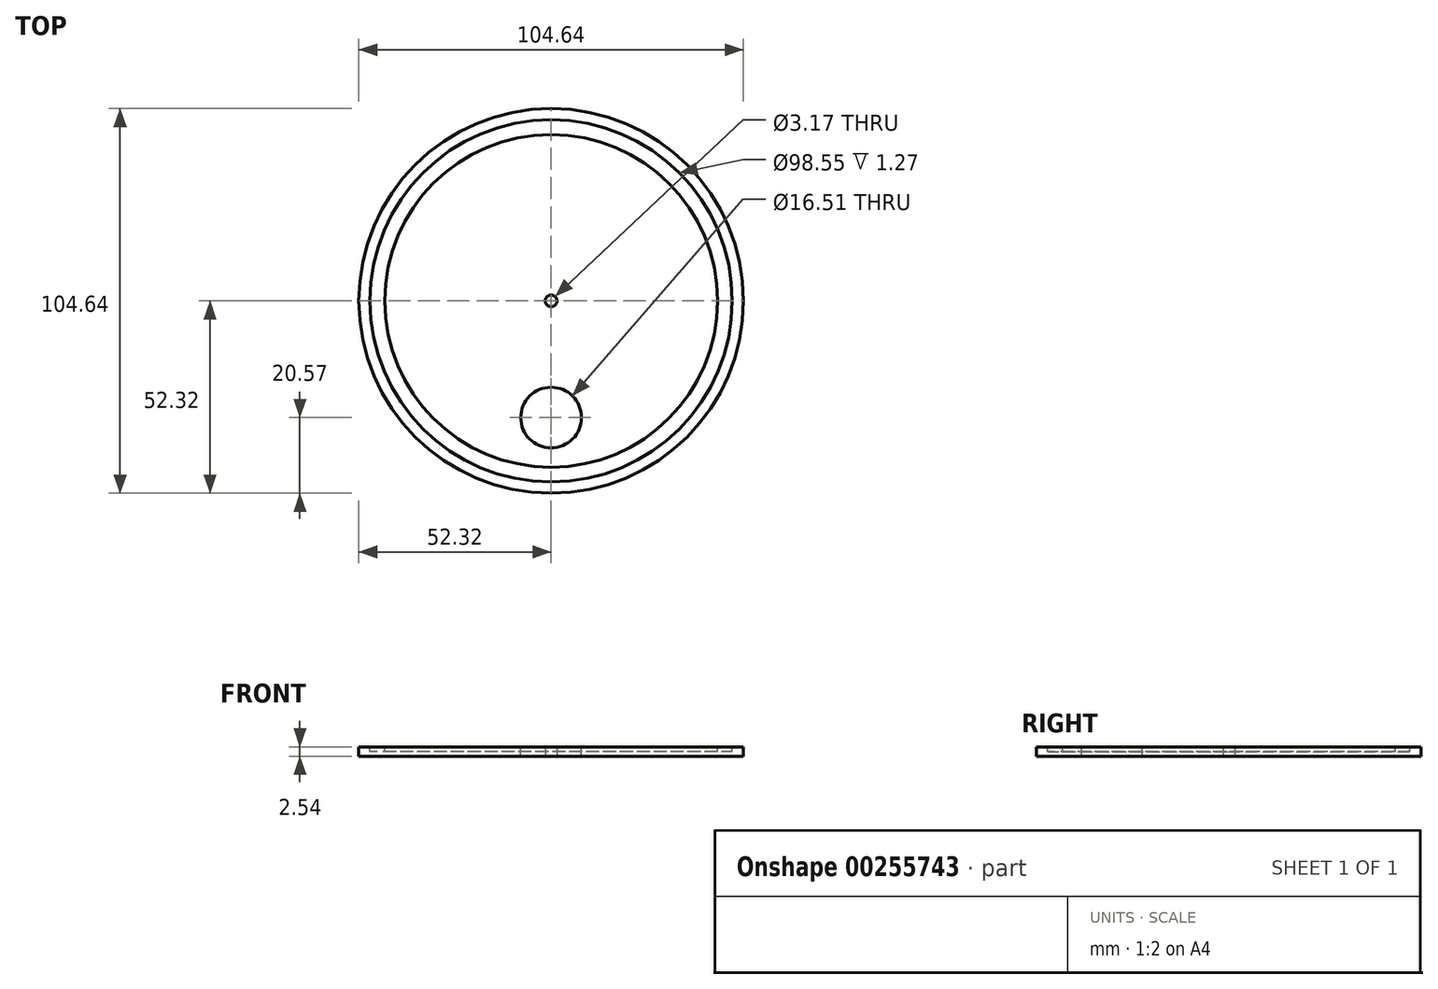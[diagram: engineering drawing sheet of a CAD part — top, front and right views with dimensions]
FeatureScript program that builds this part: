
annotation { "Feature Type Name" : "Feature", "Feature Type Description" : "" }
export const myFeature = defineFeature(function(context is Context, id is Id, definition is map)
    precondition{}
    {
        {
            var Q0;
            Q0=qCreatedBy(makeId("Top.planeOp"),FACE);
            var sketch = newSketch(context, id + "F0", { "sketchPlane" : qUnion([Q0])});
            skCircle(sketch, "E0", {"center": v(0, 0) * mm, "radius": 52.32 * mm});
            skCircle(sketch, "E1", {"center": v(0, 0) * mm, "radius": 1.59 * mm});
            skSolve(sketch);
        }
        {
            var Q0;
            Q0=makeQuery(id+"F0.imprint","IMPRINT",FACE,{"disambiguationData":[TD([[makeQuery(id+"F0.imprint","IMPRINT",EDGE,{"derivedFrom":sQuery(id+"F0.wireOp",EDGE,"E0")}),1.0]])]});
            extrude(context, id + "F1", {"entities" : qUnion([Q0]), "depth" : 2.54 * mm});
        }
        {
            var Q0;
            Q0=makeQuery(id+"F1.opExtrude","CAP_FACE",FACE,{"disambiguationData":[OSD([sQuery(id+"F0.wireOp",EDGE,"E0"),sQuery(id+"F0.wireOp",EDGE,"E1")])],"isStart":false});
            var sketch = newSketch(context, id + "F2", { "sketchPlane" : qUnion([Q0])});
            skCircle(sketch, "E2", {"center": v(0, 0) * mm, "radius": 49.28 * mm});
            skCircle(sketch, "E3", {"center": v(0, 0) * mm, "radius": 45.28 * mm});
            skSolve(sketch);
        }
        {
            var Q0;
            Q0=makeQuery(id+"F2.imprint","IMPRINT",FACE,{"disambiguationData":[TD([[makeQuery(id+"F2.imprint","IMPRINT",EDGE,{"derivedFrom":sQuery(id+"F2.wireOp",EDGE,"E2")}),1.0]])]});
            extrude(context, id + "F3", {"entities" : qUnion([Q0]), "operationType" : NewBodyOperationType.REMOVE, "oppositeDirection" : true, "depth" : 1.27 * mm});
        }
        {
            var Q0;
            {var subQ0=sQuery(id+"F0.wireOp",EDGE,"E1");Q0=makeQuery(id+"F3.boolean.opBoolean","SPLIT",FACE,{"disambiguationData":[TD([makeQuery(id+"F1.opExtrude","SWEPT_FACE",FACE,{"disambiguationData":[OSD([subQ0])]})])],"derivedFrom":makeQuery(id+"F1.opExtrude","CAP_FACE",FACE,{"disambiguationData":[OSD([sQuery(id+"F0.wireOp",EDGE,"E0"),subQ0])],"isStart":false})});}
            var sketch = newSketch(context, id + "F4", { "sketchPlane" : qUnion([Q0])});
            skCircle(sketch, "E4", {"center": v(0, -31.75) * mm, "radius": 8.26 * mm});
            skSolve(sketch);
        }
        {
            var Q0;
            Q0=makeQuery(id+"F4.imprint","IMPRINT",FACE,{"disambiguationData":[TD([[makeQuery(id+"F4.imprint","IMPRINT",EDGE,{"derivedFrom":sQuery(id+"F4.wireOp",EDGE,"E4")}),1.0]])]});
            extrude(context, id + "F5", {"entities" : qUnion([Q0]), "operationType" : NewBodyOperationType.REMOVE, "endBound" : BoundingType.THROUGH_ALL, "oppositeDirection" : true, "depth" : 25.4 * mm});
        }
    });
